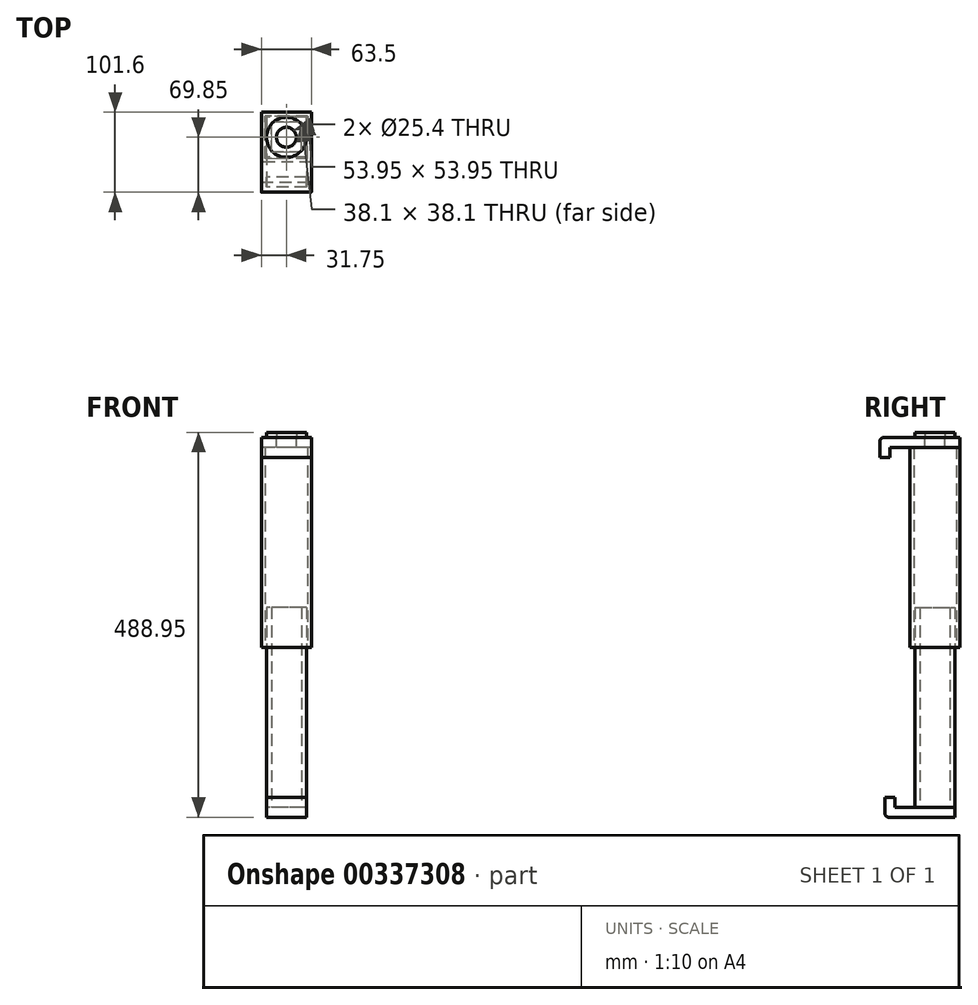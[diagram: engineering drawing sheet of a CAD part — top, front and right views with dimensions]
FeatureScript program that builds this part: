
annotation { "Feature Type Name" : "Feature", "Feature Type Description" : "" }
export const myFeature = defineFeature(function(context is Context, id is Id, definition is map)
    precondition{}
    {
        {
            var Q0;
            Q0=qCreatedBy(makeId("Top.planeOp"),FACE);
            var sketch = newSketch(context, id + "F0", { "sketchPlane" : qUnion([Q0])});
            skLineSegment(sketch, "E0.bottom", {"start": v(25.4, -25.4) * mm, "end": v(-25.4, -25.4) * mm});
            skLineSegment(sketch, "E0.top", {"start": v(25.4, 25.4) * mm, "end": v(-25.4, 25.4) * mm});
            skLineSegment(sketch, "E0.left", {"start": v(25.4, -25.4) * mm, "end": v(25.4, 25.4) * mm});
            skLineSegment(sketch, "E0.right", {"start": v(-25.4, -25.4) * mm, "end": v(-25.4, 25.4) * mm});
            skPoint(sketch, "E0.middle", {"position": v(0, 0) * mm});
            skLineSegment(sketch, "E1.0", {"start": v(19.05, 19.05) * mm, "end": v(-19.05, 19.05) * mm});
            skLineSegment(sketch, "E1.1", {"start": v(19.05, -19.05) * mm, "end": v(19.05, 19.05) * mm});
            skLineSegment(sketch, "E1.2", {"start": v(19.05, -19.05) * mm, "end": v(-19.05, -19.05) * mm});
            skLineSegment(sketch, "E1.3", {"start": v(-19.05, -19.05) * mm, "end": v(-19.05, 19.05) * mm});
            skLineSegment(sketch, "E2.bottom", {"start": v(31.75, -31.75) * mm, "end": v(-31.75, -31.75) * mm});
            skLineSegment(sketch, "E2.top", {"start": v(31.75, 31.75) * mm, "end": v(-31.75, 31.75) * mm});
            skLineSegment(sketch, "E2.left", {"start": v(31.75, -31.75) * mm, "end": v(31.75, 31.75) * mm});
            skLineSegment(sketch, "E2.right", {"start": v(-31.75, -31.75) * mm, "end": v(-31.75, 31.75) * mm});
            skLineSegment(sketch, "E3.0", {"start": v(26.97, 26.97) * mm, "end": v(-26.97, 26.97) * mm});
            skLineSegment(sketch, "E3.1", {"start": v(26.97, -26.97) * mm, "end": v(26.97, 26.97) * mm});
            skLineSegment(sketch, "E3.2", {"start": v(26.97, -26.97) * mm, "end": v(-26.97, -26.97) * mm});
            skLineSegment(sketch, "E3.3", {"start": v(-26.97, -26.97) * mm, "end": v(-26.97, 26.97) * mm});
            skSolve(sketch);
        }
        {
            var Q0;
            Q0=makeQuery(id+"F0.imprint","IMPRINT",FACE,{"disambiguationData":[TD([[makeQuery(id+"F0.imprint","IMPRINT",EDGE,{"derivedFrom":sQuery(id+"F0.wireOp",EDGE,"E0.bottom")}),-1.0]])]});
            extrude(context, id + "F1", {"entities" : qUnion([Q0]), "depth" : 254 * mm});
        }
        {
            var Q0;
            Q0=makeQuery(id+"F0.imprint","IMPRINT",FACE,{"disambiguationData":[TD([[makeQuery(id+"F0.imprint","IMPRINT",EDGE,{"derivedFrom":sQuery(id+"F0.wireOp",EDGE,"E2.bottom")}),-1.0]])]});
            extrude(context, id + "F2", {"entities" : qUnion([Q0]), "depth" : 254 * mm});
        }
        {
            var Q0;
            Q0=makeQuery(id+"F1.opExtrude","SWEPT_BODY",BODY,{"disambiguationData":[OSD([sQuery(id+"F0.wireOp",EDGE,"E0.bottom"),sQuery(id+"F0.wireOp",EDGE,"E0.top"),sQuery(id+"F0.wireOp",EDGE,"E0.left"),sQuery(id+"F0.wireOp",EDGE,"E0.right"),sQuery(id+"F0.wireOp",EDGE,"E1.0"),sQuery(id+"F0.wireOp",EDGE,"E1.1"),sQuery(id+"F0.wireOp",EDGE,"E1.2"),sQuery(id+"F0.wireOp",EDGE,"E1.3")])]});
            transform(context, id + "F3", {"entities" : qUnion([Q0]), "transformType" : TransformType.TRANSLATION_3D, "dx" : 0 * mm, "dy" : 0 * mm, "dz" : -203.2 * mm, "makeCopy" : false});
        }
        {
            var Q0;
            Q0=makeQuery(id+"F2.opExtrude","CAP_FACE",FACE,{"disambiguationData":[OSD([sQuery(id+"F0.wireOp",EDGE,"E2.bottom"),sQuery(id+"F0.wireOp",EDGE,"E2.top"),sQuery(id+"F0.wireOp",EDGE,"E2.left"),sQuery(id+"F0.wireOp",EDGE,"E2.right"),sQuery(id+"F0.wireOp",EDGE,"E3.0"),sQuery(id+"F0.wireOp",EDGE,"E3.1"),sQuery(id+"F0.wireOp",EDGE,"E3.2"),sQuery(id+"F0.wireOp",EDGE,"E3.3")])],"isStart":false});
            var sketch = newSketch(context, id + "F4", { "sketchPlane" : qUnion([Q0])});
            skLineSegment(sketch, "E4.bottom", {"start": v(-31.75, 31.75) * mm, "end": v(31.75, 31.75) * mm});
            skLineSegment(sketch, "E4.top", {"start": v(-31.75, -57.15) * mm, "end": v(31.75, -57.15) * mm});
            skLineSegment(sketch, "E4.left", {"start": v(-31.75, 31.75) * mm, "end": v(-31.75, -57.15) * mm});
            skLineSegment(sketch, "E4.right", {"start": v(31.75, 31.75) * mm, "end": v(31.75, -57.15) * mm});
            skSolve(sketch);
        }
        {
            var Q0;
            Q0 = qSketchRegion(id + "F4", true);
            extrude(context, id + "F5", {"entities" : qUnion([Q0]), "depth" : 12.7 * mm});
        }
        {
            var Q0;
            Q0=makeQuery(id+"F5.opExtrude","SWEPT_FACE",FACE,{"disambiguationData":[OSD([sQuery(id+"F4.wireOp",EDGE,"E4.top")])]});
            var sketch = newSketch(context, id + "F6", { "sketchPlane" : qUnion([Q0])});
            skPoint(sketch, "E5.oppositeSnap0", {"position": v(31.75, 260.35) * mm});
            skLineSegment(sketch, "E5.bottom", {"start": v(-31.75, 266.7) * mm, "end": v(31.75, 266.7) * mm});
            skLineSegment(sketch, "E5.top", {"start": v(-31.75, 241.3) * mm, "end": v(31.75, 241.3) * mm});
            skLineSegment(sketch, "E5.left", {"start": v(-31.75, 266.7) * mm, "end": v(-31.75, 241.3) * mm});
            skLineSegment(sketch, "E5.right", {"start": v(31.75, 266.7) * mm, "end": v(31.75, 241.3) * mm});
            skSolve(sketch);
        }
        {
            var Q0;
            Q0 = qSketchRegion(id + "F6", true);
            extrude(context, id + "F7", {"entities" : qUnion([Q0]), "operationType" : NewBodyOperationType.ADD, "depth" : 12.7 * mm});
        }
        {
            var Q0;
            Q0=makeQuery(id+"F7.boolean.opBoolean","MERGE",FACE,{"derivedFrom":[makeQuery(id+"F5.opExtrude","CAP_FACE",FACE,{"disambiguationData":[OSD([sQuery(id+"F4.wireOp",EDGE,"E4.bottom"),sQuery(id+"F4.wireOp",EDGE,"E4.top"),sQuery(id+"F4.wireOp",EDGE,"E4.left"),sQuery(id+"F4.wireOp",EDGE,"E4.right")])],"isStart":false}),makeQuery(id+"F7.opExtrude","SWEPT_FACE",FACE,{"disambiguationData":[OSD([sQuery(id+"F6.wireOp",EDGE,"E5.bottom")])]})]});
            var sketch = newSketch(context, id + "F8", { "sketchPlane" : qUnion([Q0])});
            skCircle(sketch, "E6", {"center": v(0, 0) * mm, "radius": 12.7 * mm});
            skSolve(sketch);
        }
        {
            var Q0;
            Q0 = qSketchRegion(id + "F8", true);
            extrude(context, id + "F9", {"entities" : qUnion([Q0]), "operationType" : NewBodyOperationType.REMOVE, "oppositeDirection" : true, "depth" : 25.4 * mm});
        }
        {
            var Q0;
            Q0=makeQuery(id+"F1.opExtrude","CAP_FACE",FACE,{"disambiguationData":[OSD([sQuery(id+"F0.wireOp",EDGE,"E0.bottom"),sQuery(id+"F0.wireOp",EDGE,"E0.top"),sQuery(id+"F0.wireOp",EDGE,"E0.left"),sQuery(id+"F0.wireOp",EDGE,"E0.right"),sQuery(id+"F0.wireOp",EDGE,"E1.0"),sQuery(id+"F0.wireOp",EDGE,"E1.1"),sQuery(id+"F0.wireOp",EDGE,"E1.2"),sQuery(id+"F0.wireOp",EDGE,"E1.3")])],"isStart":true});
            var sketch = newSketch(context, id + "F10", { "sketchPlane" : qUnion([Q0])});
            skLineSegment(sketch, "E7.bottom", {"start": v(25.4, -25.4) * mm, "end": v(-25.4, -25.4) * mm});
            skLineSegment(sketch, "E7.top", {"start": v(25.4, 50.8) * mm, "end": v(-25.4, 50.8) * mm});
            skLineSegment(sketch, "E7.left", {"start": v(25.4, -25.4) * mm, "end": v(25.4, 50.8) * mm});
            skLineSegment(sketch, "E7.right", {"start": v(-25.4, -25.4) * mm, "end": v(-25.4, 50.8) * mm});
            skSolve(sketch);
        }
        {
            var Q0;
            Q0 = qSketchRegion(id + "F10", true);
            extrude(context, id + "F11", {"entities" : qUnion([Q0]), "depth" : 12.7 * mm});
        }
        {
            var Q0;
            Q0=makeQuery(id+"F11.opExtrude","SWEPT_FACE",FACE,{"disambiguationData":[OSD([sQuery(id+"F10.wireOp",EDGE,"E7.top")])]});
            var sketch = newSketch(context, id + "F12", { "sketchPlane" : qUnion([Q0])});
            skLineSegment(sketch, "E8.bottom", {"start": v(25.4, -215.9) * mm, "end": v(-25.4, -215.9) * mm});
            skLineSegment(sketch, "E8.top", {"start": v(25.4, -190.5) * mm, "end": v(-25.4, -190.5) * mm});
            skLineSegment(sketch, "E8.left", {"start": v(25.4, -215.9) * mm, "end": v(25.4, -190.5) * mm});
            skLineSegment(sketch, "E8.right", {"start": v(-25.4, -215.9) * mm, "end": v(-25.4, -190.5) * mm});
            skSolve(sketch);
        }
        {
            var Q0;
            Q0 = qSketchRegion(id + "F12", true);
            extrude(context, id + "F13", {"entities" : qUnion([Q0]), "operationType" : NewBodyOperationType.ADD, "depth" : 12.7 * mm});
        }
        {
            var Q0;
            Q0=makeQuery(id+"F13.opExtrude","CAP_EDGE",EDGE,{"disambiguationData":[OSD([sQuery(id+"F12.wireOp",EDGE,"E8.bottom")])],"isStart":false});
            fillet(context, id + "F14", {"entities" : qUnion([Q0]), "radius" : 5.08 * mm, "tangentPropagation" : true, "allowEdgeOverflow" : false});
        }
        {
            var Q0;
            Q0=makeQuery(id+"F7.opExtrude","CAP_EDGE",EDGE,{"disambiguationData":[OSD([sQuery(id+"F6.wireOp",EDGE,"E5.bottom")])],"isStart":false});
            fillet(context, id + "F15", {"entities" : qUnion([Q0]), "radius" : 5.08 * mm, "tangentPropagation" : true, "allowEdgeOverflow" : false});
        }
        {
            var Q0;
            Q0=makeQuery(id+"F7.boolean.opBoolean","MERGE",FACE,{"derivedFrom":[makeQuery(id+"F5.opExtrude","CAP_FACE",FACE,{"disambiguationData":[OSD([sQuery(id+"F4.wireOp",EDGE,"E4.bottom"),sQuery(id+"F4.wireOp",EDGE,"E4.top"),sQuery(id+"F4.wireOp",EDGE,"E4.left"),sQuery(id+"F4.wireOp",EDGE,"E4.right")])],"isStart":false}),makeQuery(id+"F7.opExtrude","SWEPT_FACE",FACE,{"disambiguationData":[OSD([sQuery(id+"F6.wireOp",EDGE,"E5.bottom")])]})]});
            var sketch = newSketch(context, id + "F16", { "sketchPlane" : qUnion([Q0])});
            skCircle(sketch, "E9", {"center": v(0, 0) * mm, "radius": 25.4 * mm});
            skSolve(sketch);
        }
        {
            var Q0;
            Q0=makeQuery(id+"F16.imprint","IMPRINT",FACE,{"disambiguationData":[TD([[makeQuery(id+"F16.imprint","IMPRINT",EDGE,{"derivedFrom":sQuery(id+"F16.wireOp",EDGE,"E9")}),1.0]])]});
            extrude(context, id + "F17", {"entities" : qUnion([Q0]), "depth" : 6.35 * mm});
        }
    });
